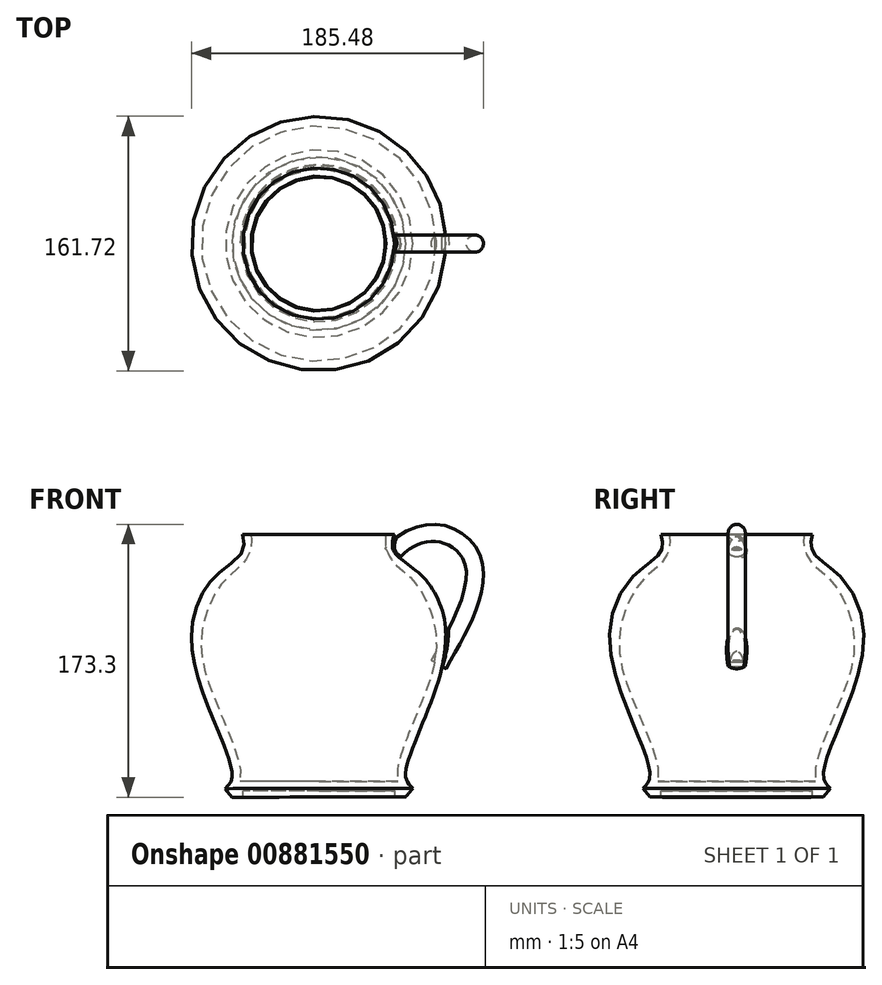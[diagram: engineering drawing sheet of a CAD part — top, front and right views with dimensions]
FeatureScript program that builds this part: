
annotation { "Feature Type Name" : "Feature", "Feature Type Description" : "" }
export const myFeature = defineFeature(function(context is Context, id is Id, definition is map)
    precondition{}
    {
        {
            var Q0;
            Q0=qCreatedBy(makeId("Front.planeOp"),FACE);
            var sketch = newSketch(context, id + "F0", { "sketchPlane" : qUnion([Q0])});
            skLineSegment(sketch, "E0", {"start": v(136.86, -48.2) * mm, "end": v(86.37, -48.2) * mm});
            skLineSegment(sketch, "E1", {"start": v(86.37, -48.2) * mm, "end": v(86.37, -54.23) * mm});
            skLineSegment(sketch, "E2", {"start": v(86.37, -54.23) * mm, "end": v(134.95, -54.23) * mm});
            skLineSegment(sketch, "E3", {"start": v(134.95, -54.23) * mm, "end": v(134.95, -58.15) * mm});
            skLineSegment(sketch, "E4", {"start": v(134.95, -58.15) * mm, "end": v(141.87, -58.15) * mm});
            skLineSegment(sketch, "E5", {"start": v(141.87, -58.15) * mm, "end": v(146.32, -52.68) * mm});
            skLineSegment(sketch, "E6", {"start": v(129.36, 108.63) * mm, "end": v(134.6, 108.63) * mm});
            skFitSpline(sketch, "E7", {"points": [v(146.32, -52.68) * mm, v(141.87, -45.71) * mm, v(151.65, -13.45) * mm, v(167.41, 43.66) * mm, v(152.62, 81.72) * mm, v(134.95, 97.32) * mm, v(134.6, 108.63) * mm], "startDerivative": vector(-69.95, 69.83) * mm, "endDerivative": vector(29.91, 101.88) * mm});
            skFitSpline(sketch, "E8", {"points": [v(129.36, 108.63) * mm, v(129.36, 100.02) * mm, v(134.37, 90.46) * mm, v(146.32, 79.5) * mm, v(159.01, 55.1) * mm, v(160.17, 27.6) * mm, v(148.94, -4.93) * mm, v(136.86, -38.89) * mm, v(136.86, -48.2) * mm], "startDerivative": vector(-20.86, -91.75) * mm, "endDerivative": vector(12.38, -86.65) * mm});
            skLineSegment(sketch, "E9", {"start": v(86.75, -58.34) * mm, "end": v(86.37, 135.1) * mm});
            skSolve(sketch);
        }
        {
            var Q0;
            {var subQ0=sQuery(id+"F0.wireOp",EDGE,"E3");Q0=makeQuery(id+"F0.imprint","IMPRINT",FACE,{"disambiguationData":[TD([[makeQuery(id+"F0.imprint","IMPRINT",EDGE,{"derivedFrom":subQ0}),1.0]])]});}
            var Q1;
            Q1=sQuery(id+"F0.wireOp",EDGE,"E9");
            revolve(context, id + "F1", {"surfaceOperationType" : NewSurfaceOperationType.NEW, "entities" : qUnion([Q0]), "axis" : qUnion([Q1]), "revolveType" : RevolveType.FULL, "oppositeDirection" : true});
        }
        {
            var Q0;
            Q0=qCreatedBy(makeId("Front.planeOp"),FACE);
            var sketch = newSketch(context, id + "F2", { "sketchPlane" : qUnion([Q0])});
            skFitSpline(sketch, "E10", {"points": [v(162.66, 25.92) * mm, v(183.37, 68.4) * mm, v(183.06, 95.4) * mm, v(163.97, 109.18) * mm, v(142.75, 104.97) * mm, v(132.59, 96.12) * mm], "startDerivative": vector(92.02, 160.4) * mm, "endDerivative": vector(-59.38, -64.96) * mm});
            skSolve(sketch);
        }
        {
            var Q0;
            Q0=sQuery(id+"F2.wireOp",EDGE,"E10");
            var Q1;
            Q1=sQuery(id+"F2.wireOp",VERTEX,"E10.start");
            cPlane(context, id + "F3", {"entities" : qUnion([Q0, Q1]), "cplaneType" : CPlaneType.CURVE_POINT, "offset" : 25 * mm, "width" : 150 * mm, "height" : 150 * mm});
        }
        {
            var Q0;
            Q0=qCreatedBy(id+"F3.planeOp",FACE);
            var sketch = newSketch(context, id + "F4", { "sketchPlane" : qUnion([Q0])});
            skCircle(sketch, "E11", {"center": v(128.14, 0) * mm, "radius": 5.43 * mm});
            skSolve(sketch);
        }
        {
            var Q0;
            Q0=makeQuery(id+"F4.imprint","IMPRINT",FACE,{"disambiguationData":[TD([[makeQuery(id+"F4.imprint","IMPRINT",EDGE,{"derivedFrom":sQuery(id+"F4.wireOp",EDGE,"E11")}),1.0]])]});
            var Q1;
            Q1=sQuery(id+"F2.wireOp",EDGE,"E10");
            sweep(context, id + "F5", {"operationType" : NewBodyOperationType.ADD, "profiles" : qUnion([Q0]), "path" : qUnion([Q1])});
        }
        {
            var Q0;
            Q0=makeQuery(id+"F5.boolean.opBoolean","INTERSECT",EDGE,{"disambiguationData":[OD(1.0)],"derivedFrom":[makeQuery(id+"F1.opRevolve","SWEPT_FACE",FACE,{"disambiguationData":[OSD([sQuery(id+"F0.wireOp",EDGE,"E7")])]}),makeQuery(id+"F5.opSweep","SWEPT_FACE",FACE,{"disambiguationData":[OSD([sQuery(id+"F2.wireOp",EDGE,"E10"),sQuery(id+"F4.wireOp",EDGE,"E11")])]})]});
            var Q1;
            Q1=makeQuery(id+"F5.boolean.opBoolean","INTERSECT",EDGE,{"disambiguationData":[OD(0.0)],"derivedFrom":[makeQuery(id+"F1.opRevolve","SWEPT_FACE",FACE,{"disambiguationData":[OSD([sQuery(id+"F0.wireOp",EDGE,"E7")])]}),makeQuery(id+"F5.opSweep","SWEPT_FACE",FACE,{"disambiguationData":[OSD([sQuery(id+"F2.wireOp",EDGE,"E10"),sQuery(id+"F4.wireOp",EDGE,"E11")])]})]});
            fillet(context, id + "F6", {"entities" : qUnion([Q0, Q1]), "radius" : 1.09 * mm, "tangentPropagation" : true, "allowEdgeOverflow" : false});
        }
    });
